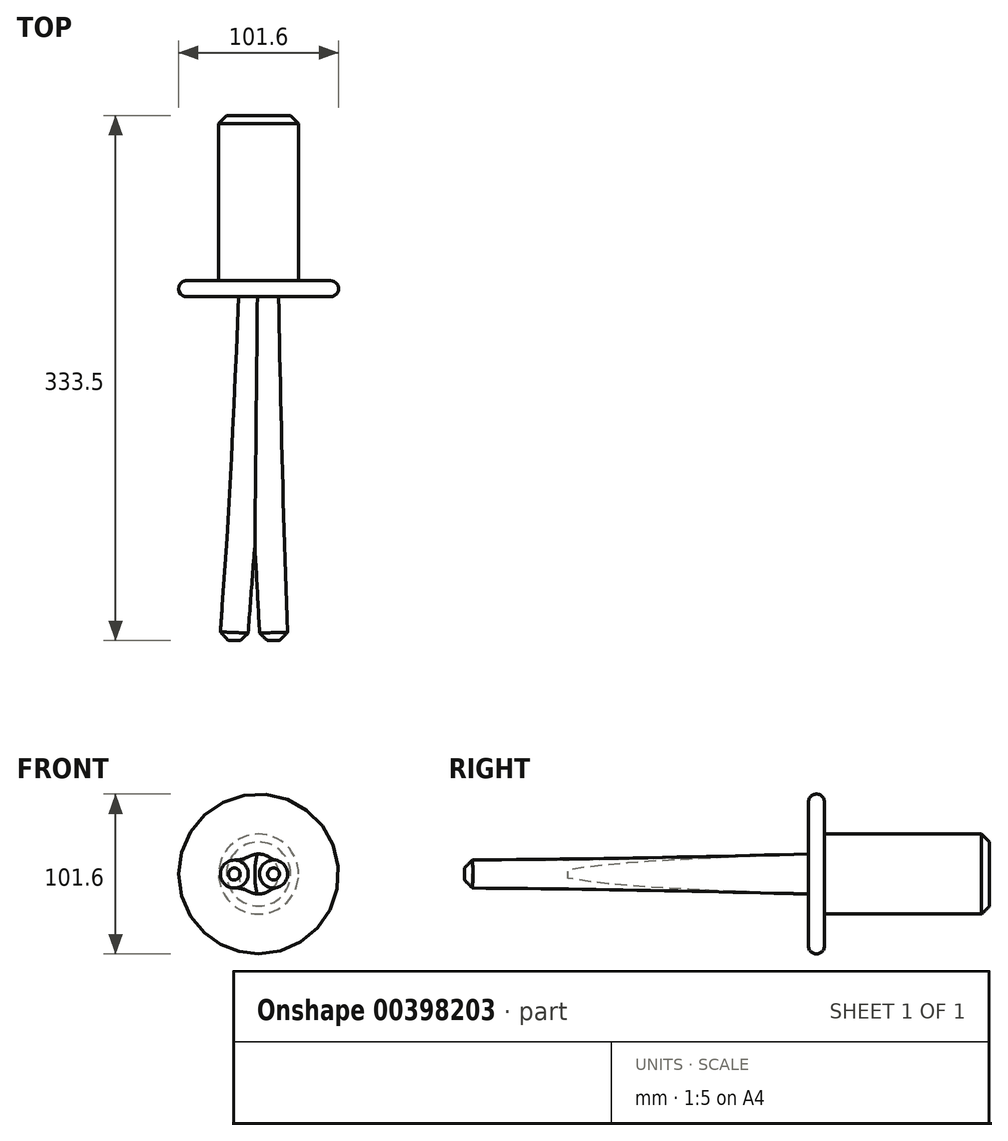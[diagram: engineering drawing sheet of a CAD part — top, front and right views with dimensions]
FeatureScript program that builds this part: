
annotation { "Feature Type Name" : "Feature", "Feature Type Description" : "" }
export const myFeature = defineFeature(function(context is Context, id is Id, definition is map)
    precondition{}
    {
        {
            var Q0;
            Q0=qCreatedBy(makeId("Front.planeOp"),FACE);
            cPlane(context, id + "F0", {"entities" : qUnion([Q0]), "cplaneType" : CPlaneType.OFFSET, "offset" : 104.9 * mm, "width" : 152.4 * mm, "height" : 152.4 * mm});
        }
        {
            var Q0;
            Q0=qCreatedBy(id+"F0.planeOp",FACE);
            cPlane(context, id + "F1", {"entities" : qUnion([Q0]), "cplaneType" : CPlaneType.OFFSET, "offset" : 10.16 * mm, "width" : 152.4 * mm, "height" : 152.4 * mm});
        }
        {
            var Q0;
            Q0=qCreatedBy(id+"F1.planeOp",FACE);
            cPlane(context, id + "F2", {"entities" : qUnion([Q0]), "cplaneType" : CPlaneType.OFFSET, "offset" : 218.44 * mm, "width" : 152.4 * mm, "height" : 152.4 * mm});
        }
        {
            var Q0;
            Q0=qCreatedBy(makeId("Front.planeOp"),FACE);
            var sketch = newSketch(context, id + "F3", { "sketchPlane" : qUnion([Q0])});
            skCircle(sketch, "E0", {"center": v(0, 0) * mm, "radius": 25.4 * mm});
            skSolve(sketch);
        }
        {
            var Q0;
            Q0=qCreatedBy(id+"F0.planeOp",FACE);
            var sketch = newSketch(context, id + "F4", { "sketchPlane" : qUnion([Q0])});
            skCircle(sketch, "E1", {"center": v(0, 0) * mm, "radius": 25.4 * mm});
            skSolve(sketch);
        }
        {
            var Q0;
            Q0=qCreatedBy(id+"F0.planeOp",FACE);
            var sketch = newSketch(context, id + "F5", { "sketchPlane" : qUnion([Q0])});
            skCircle(sketch, "E2", {"center": v(0, 0) * mm, "radius": 50.8 * mm});
            skSolve(sketch);
        }
        {
            var Q0;
            Q0=qCreatedBy(id+"F1.planeOp",FACE);
            var sketch = newSketch(context, id + "F6", { "sketchPlane" : qUnion([Q0])});
            skCircle(sketch, "E3", {"center": v(0, 0) * mm, "radius": 50.8 * mm});
            skSolve(sketch);
        }
        {
            var Q0;
            Q0=qCreatedBy(id+"F1.planeOp",FACE);
            var sketch = newSketch(context, id + "F7", { "sketchPlane" : qUnion([Q0])});
            skCircle(sketch, "E4", {"center": v(0, 0) * mm, "radius": 12.7 * mm});
            skSolve(sketch);
        }
        {
            var Q0;
            Q0 = qSketchRegion(id + "F4", true);
            var Q1;
            Q1=makeQuery(id+"F3.imprint","IMPRINT",FACE,{"disambiguationData":[TD([[makeQuery(id+"F3.imprint","IMPRINT",EDGE,{"derivedFrom":sQuery(id+"F3.wireOp",EDGE,"E0")}),1.0]])]});
            loft(context, id + "F8", {"sheetProfilesArray" : [{ "sheetProfileEntities" : qUnion([Q0]) }, { "sheetProfileEntities" : qUnion([Q1]) }]});
        }
        {
            var Q1;
            Q1 = qSketchRegion(id + "F5", true);
            var Q2;
            Q2 = qSketchRegion(id + "F6", true);
            loft(context, id + "F9", {"operationType" : NewBodyOperationType.ADD, "sheetProfilesArray" : [{ "sheetProfileEntities" : qUnion([Q1]) }, { "sheetProfileEntities" : qUnion([Q2]) }]});
        }
        {
            var Q0;
            Q0=qCreatedBy(id+"F2.planeOp",FACE);
            var sketch = newSketch(context, id + "F10", { "sketchPlane" : qUnion([Q0])});
            skCircle(sketch, "E5", {"center": v(-15.78, 0) * mm, "radius": 8.9 * mm});
            skCircle(sketch, "E6", {"center": v(15.56, 0) * mm, "radius": 8.9 * mm});
            skSolve(sketch);
        }
        {
            var Q1;
            Q1=makeQuery(id+"F7.imprint","IMPRINT",FACE,{"disambiguationData":[TD([[makeQuery(id+"F7.imprint","IMPRINT",EDGE,{"derivedFrom":sQuery(id+"F7.wireOp",EDGE,"E4")}),1.0]])]});
            var Q2;
            Q2=makeQuery(id+"F10.imprint","IMPRINT",FACE,{"disambiguationData":[TD([[makeQuery(id+"F10.imprint","IMPRINT",EDGE,{"derivedFrom":sQuery(id+"F10.wireOp",EDGE,"E5")}),1.0]])]});
            loft(context, id + "F11", {"operationType" : NewBodyOperationType.ADD, "sheetProfilesArray" : [{ "sheetProfileEntities" : qUnion([Q1]) }, { "sheetProfileEntities" : qUnion([Q2]) }]});
        }
        {
            var Q0;
            Q0=qCreatedBy(id+"F2.planeOp",FACE);
            cPlane(context, id + "F12", {"entities" : qUnion([Q0]), "cplaneType" : CPlaneType.OFFSET, "offset" : 0 * mm, "width" : 152.4 * mm, "height" : 152.4 * mm});
        }
        {
            var Q0;
            Q0=qCreatedBy(id+"F12.planeOp",FACE);
            var sketch = newSketch(context, id + "F13", { "sketchPlane" : qUnion([Q0])});
            skCircle(sketch, "E7", {"center": v(9.76, 0) * mm, "radius": 8.9 * mm});
            skSolve(sketch);
        }
        {
            var Q0;
            Q0=qCreatedBy(id+"F1.planeOp",FACE);
            cPlane(context, id + "F14", {"entities" : qUnion([Q0]), "cplaneType" : CPlaneType.OFFSET, "offset" : 0 * mm, "width" : 152.4 * mm, "height" : 152.4 * mm});
        }
        {
            var Q0;
            Q0=qCreatedBy(id+"F14.planeOp",FACE);
            var sketch = newSketch(context, id + "F15", { "sketchPlane" : qUnion([Q0])});
            skCircle(sketch, "E8", {"center": v(0, 0) * mm, "radius": 12.7 * mm});
            skSolve(sketch);
        }
        {
            var Q1;
            Q1 = qSketchRegion(id + "F15", true);
            var Q2;
            Q2 = qSketchRegion(id + "F13", true);
            loft(context, id + "F16", {"operationType" : NewBodyOperationType.ADD, "sheetProfilesArray" : [{ "sheetProfileEntities" : qUnion([Q1]) }, { "sheetProfileEntities" : qUnion([Q2]) }]});
        }
        {
            var Q0;
            Q0=makeQuery(id+"F11.opLoft","MID_CAP_EDGE",EDGE,{"disambiguationData":[OSD([sQuery(id+"F7.wireOp",EDGE,"E4"),sQuery(id+"F10.wireOp",EDGE,"E5")])],"capPos":1.0});
            var Q1;
            Q1=makeQuery(id+"F16.opLoft","MID_CAP_EDGE",EDGE,{"disambiguationData":[OSD([sQuery(id+"F13.wireOp",EDGE,"E7"),sQuery(id+"F15.wireOp",EDGE,"E8")])],"capPos":1.0});
            chamfer(context, id + "F17", {"entities" : qUnion([Q0, Q1]), "width" : 5.08 * mm, "tangentPropagation" : true});
        }
        {
            var Q0;
            Q0=makeQuery(id+"F9.opLoft","MID_CAP_EDGE",EDGE,{"disambiguationData":[OSD([sQuery(id+"F5.wireOp",EDGE,"E2"),sQuery(id+"F6.wireOp",EDGE,"E3")])],"capPos":1.0});
            var Q1;
            Q1=makeQuery(id+"F9.opLoft","MID_CAP_EDGE",EDGE,{"disambiguationData":[OSD([sQuery(id+"F5.wireOp",EDGE,"E2")])],"capPos":0.0});
            fillet(context, id + "F18", {"entities" : qUnion([Q0, Q1]), "radius" : 5.08 * mm, "tangentPropagation" : true, "allowEdgeOverflow" : false});
        }
        {
            var Q0;
            Q0=makeQuery(id+"F8.opLoft","MID_CAP_EDGE",EDGE,{"disambiguationData":[OSD([sQuery(id+"F3.wireOp",EDGE,"E0"),sQuery(id+"F4.wireOp",EDGE,"E1")])],"capPos":1.0});
            chamfer(context, id + "F19", {"entities" : qUnion([Q0]), "width" : 5.08 * mm, "tangentPropagation" : true});
        }
    });
